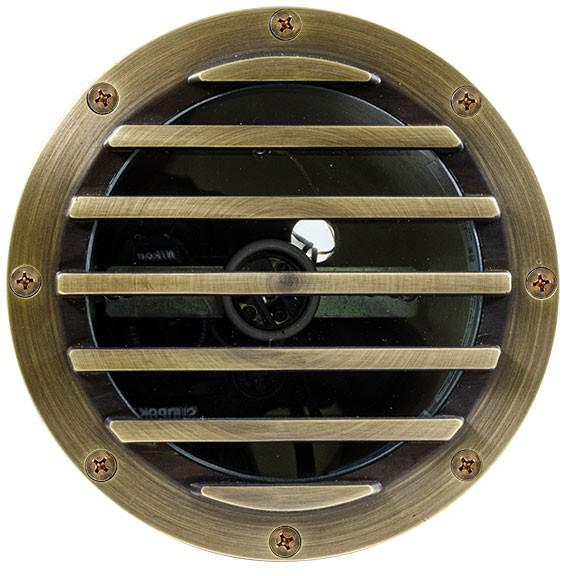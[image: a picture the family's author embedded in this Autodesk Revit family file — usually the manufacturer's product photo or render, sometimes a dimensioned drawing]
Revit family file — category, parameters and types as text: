
# Revit family: Alcon-9034-12-Revit-Family
name_source: partatom
category: Luminarias
units: mm (PartAtom-declared; Revit-internal decimal feet)

## family parameters
Anfitrión = Cara
Compartido = No
Corte con vacíos al cargar = No
Cota de conector redondo = Usar diámetro
Mantener orientación de anotación = No
Origen de luz = Sí
Punto de cálculo de habitación = No
Tipo de pieza = Normal

## types (1)
- Alcon-9034-12-Revit-Family
    Cambio de temperatura de color de luz atenuada = <Ninguno>
    Elevación por defecto = 4' - 0"
    Fabricante = Alcon Lighting
    Filtro de color = 16777215
    GLASS LENS = Analytical Panels
    HOUSING = <Por categoría>
    LENS GLASS = Glass
    Link to IES File = https://www.alconlighting.com
    Longitud de símbolo de origen de luz = 10' - 0"
    Modelo = Alcon Lighting 9034-12
    Product Data URL = https://www.alconlighting.com
    Product Page = https://www.alconlighting.com
    TAP LENS = <Por categoría>
    TOP FINISH = <Por categoría>
    URL = https://www.alconlighting.com
    Ángulo de campo de foco = 90.00°
    Ángulo de enfoque = 30.00°
    Ángulo de inclinación = 60.00°

## geometry (parser evidence)
native form markers: Sweep x3
no freeform markers — native parametric forms only
